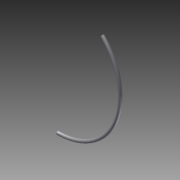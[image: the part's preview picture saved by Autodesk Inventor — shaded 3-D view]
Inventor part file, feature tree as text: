
AUTODESK INVENTOR PART (.ipt)
format: ipt  version: 2012 (Build 160160000, 160)  size: 91,136 bytes
history: native  units: in
note: dims shown in document units (in); Inventor stores cm internally (conversion verified against a paired STEP export)
features: sketch x2, sweep x1
ambient origin geometry x8: Origin, YZ Plane, XZ Plane, XY Plane, X Axis, Y Axis, Z Axis, Center Point
bodies: Solid1 (feature_tree)
feature tree (3):
  sweep  "Sweep1"
  sketch  "Sketch1"  dims[d0=7.0in d1=135.0deg]
  sketch  "Sketch2"  dims[d2=0.375in d3=0.3125in d4=0.0in]
